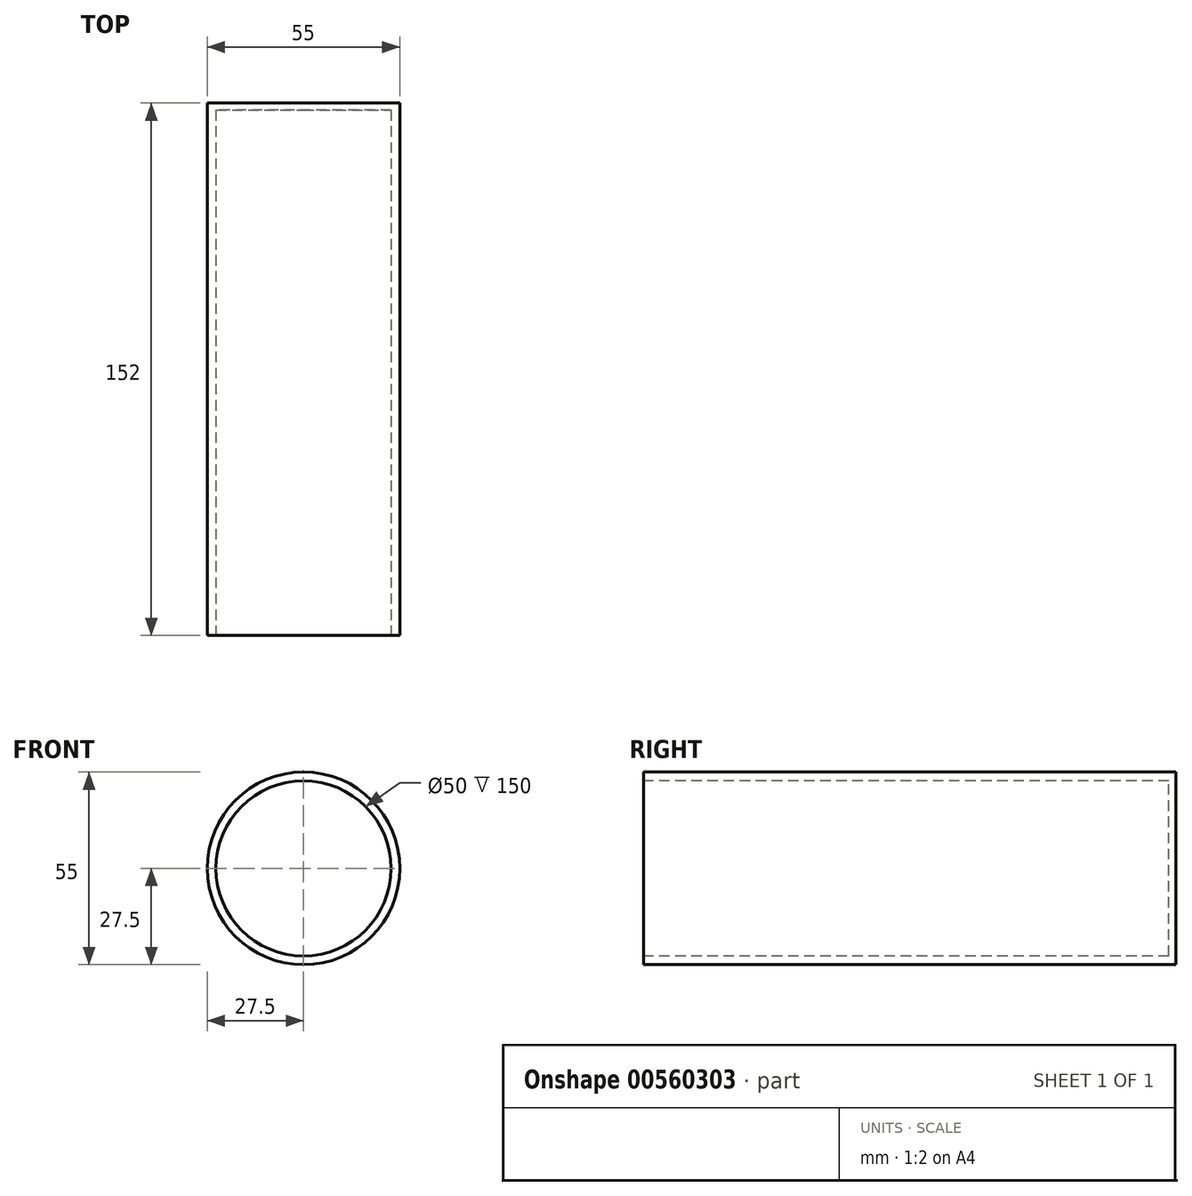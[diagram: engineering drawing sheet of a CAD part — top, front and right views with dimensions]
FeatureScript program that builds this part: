
annotation { "Feature Type Name" : "Feature", "Feature Type Description" : "" }
export const myFeature = defineFeature(function(context is Context, id is Id, definition is map)
    precondition{}
    {
        {
            var Q0;
            Q0=qCreatedBy(makeId("Front.planeOp"),FACE);
            var sketch = newSketch(context, id + "F0", { "sketchPlane" : qUnion([Q0])});
            skCircle(sketch, "E0", {"center": v(0, 0) * mm, "radius": 27.5 * mm});
            skSolve(sketch);
        }
        {
            var Q0;
            Q0 = qSketchRegion(id + "F0", true);
            extrude(context, id + "F1", {"entities" : qUnion([Q0]), "endBound" : BoundingType.SYMMETRIC, "depth" : 152 * mm, "offsetDistance" : 25 * mm});
        }
        {
            var Q0;
            Q0=makeQuery(id+"F1.opExtrude","CAP_FACE",FACE,{"disambiguationData":[OSD([sQuery(id+"F0.wireOp",EDGE,"E0")])],"isStart":false});
            var sketch = newSketch(context, id + "F2", { "sketchPlane" : qUnion([Q0])});
            skCircle(sketch, "E1", {"center": v(0, 0) * mm, "radius": 25 * mm});
            skSolve(sketch);
        }
        {
            var Q0;
            Q0 = qSketchRegion(id + "F2", true);
            extrude(context, id + "F3", {"entities" : qUnion([Q0]), "operationType" : NewBodyOperationType.REMOVE, "oppositeDirection" : true, "depth" : 150 * mm, "offsetDistance" : 25 * mm});
        }
    });
